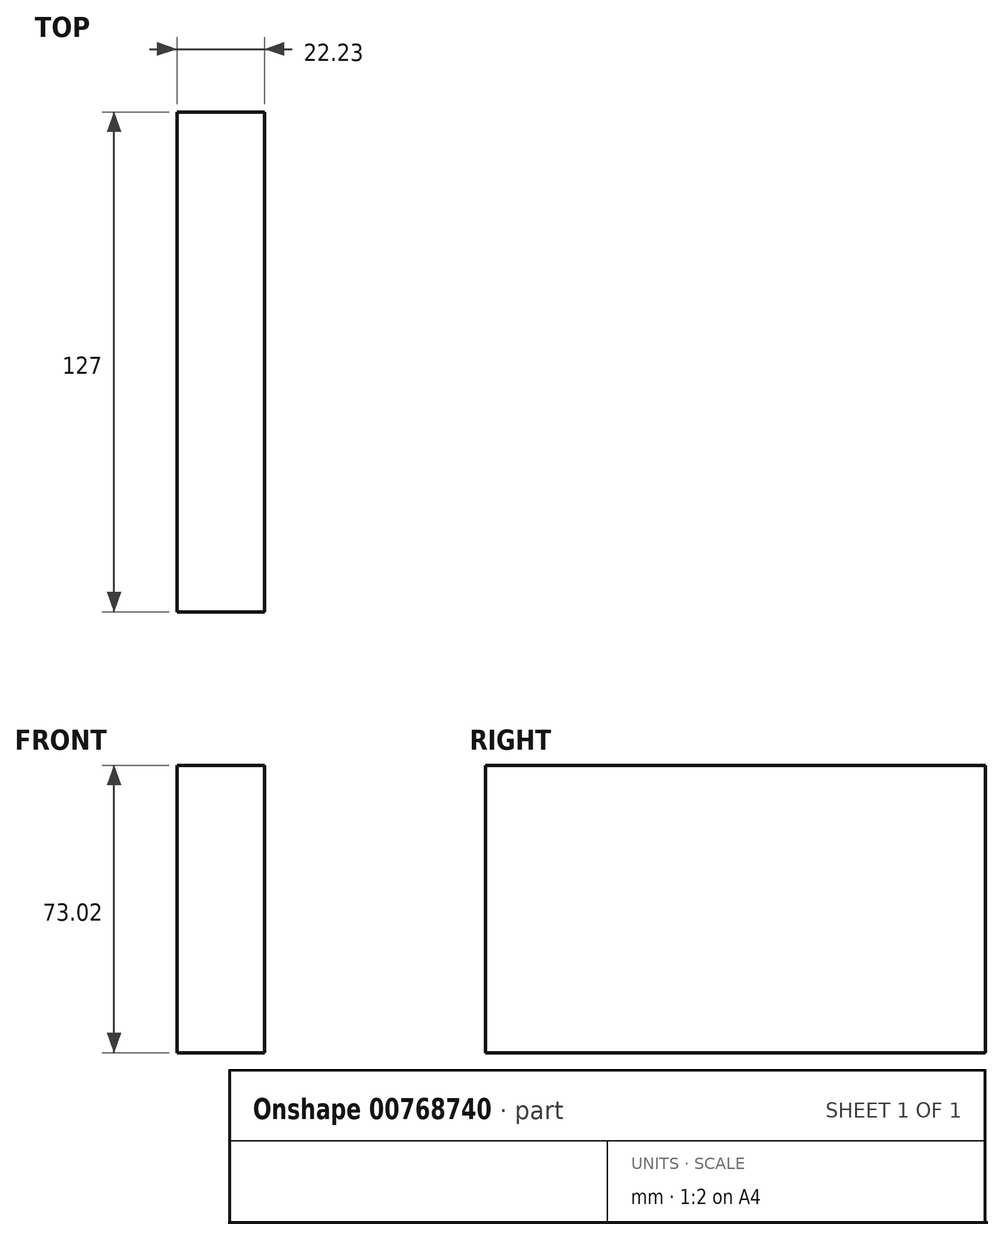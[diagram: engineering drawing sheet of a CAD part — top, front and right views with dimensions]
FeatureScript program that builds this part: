
annotation { "Feature Type Name" : "Feature", "Feature Type Description" : "" }
export const myFeature = defineFeature(function(context is Context, id is Id, definition is map)
    precondition{}
    {
        {
            var Q0;
            Q0=qCreatedBy(makeId("Front.planeOp"),FACE);
            var sketch = newSketch(context, id + "F0", { "sketchPlane" : qUnion([Q0])});
            skLineSegment(sketch, "E0", {"start": v(-26.02, 34.18) * mm, "end": v(-3.8, 34.18) * mm});
            skLineSegment(sketch, "E1", {"start": v(-3.8, 34.18) * mm, "end": v(-3.8, -38.84) * mm});
            skLineSegment(sketch, "E2", {"start": v(-3.8, -38.84) * mm, "end": v(-26.02, -38.84) * mm});
            skLineSegment(sketch, "E3", {"start": v(-26.02, -38.84) * mm, "end": v(-26.02, 34.18) * mm});
            skSolve(sketch);
        }
        {
            var Q0;
            Q0=makeQuery(id+"F0.imprint","IMPRINT",FACE,{"disambiguationData":[TD([[makeQuery(id+"F0.imprint","IMPRINT",EDGE,{"derivedFrom":sQuery(id+"F0.wireOp",EDGE,"E0")}),-1.0]])]});
            extrude(context, id + "F1", {"entities" : qUnion([Q0]), "depth" : 127 * mm, "offsetDistance" : 25.4 * mm});
        }
    });
